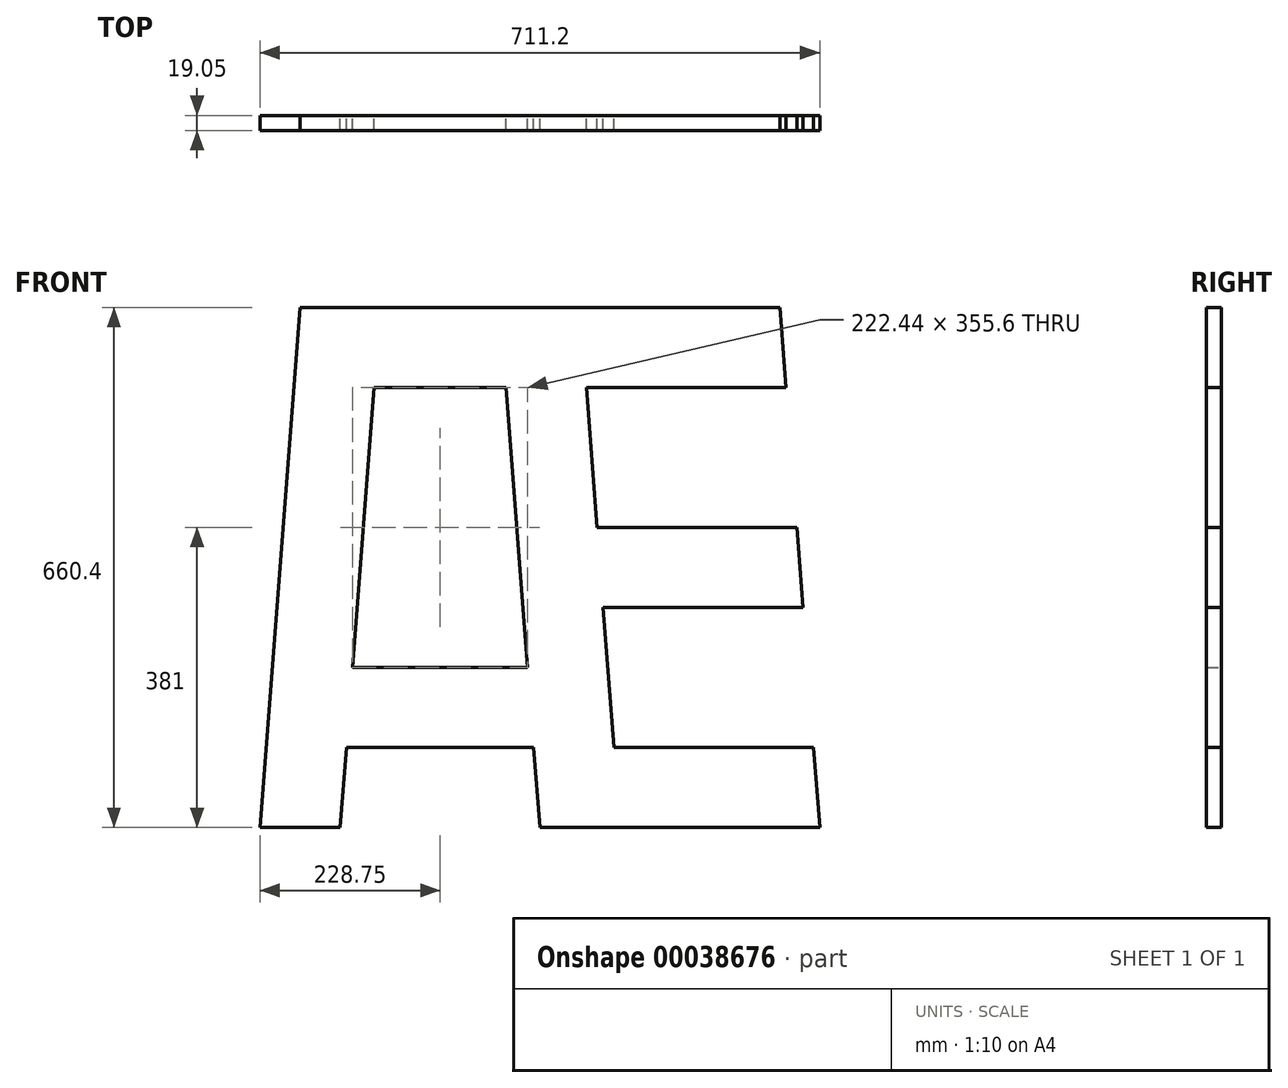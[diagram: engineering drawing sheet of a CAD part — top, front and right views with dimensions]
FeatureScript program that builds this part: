
annotation { "Feature Type Name" : "Feature", "Feature Type Description" : "" }
export const myFeature = defineFeature(function(context is Context, id is Id, definition is map)
    precondition{}
    {
        {
            var Q0;
            Q0=qCreatedBy(makeId("Front.planeOp"),FACE);
            var sketch = newSketch(context, id + "F0", { "sketchPlane" : qUnion([Q0])});
            skLineSegment(sketch, "E0", {"start": v(-304.8, 660.4) * mm, "end": v(-355.6, 0) * mm});
            skLineSegment(sketch, "E1", {"start": v(-355.6, 0) * mm, "end": v(355.6, 0) * mm});
            skLineSegment(sketch, "E2", {"start": v(355.6, 0) * mm, "end": v(304.8, 660.4) * mm});
            skLineSegment(sketch, "E3", {"start": v(304.8, 660.4) * mm, "end": v(-304.8, 660.4) * mm});
            skLineSegment(sketch, "E4", {"start": v(0, 660.4) * mm, "end": v(0, 0) * mm, "construction": true});
            skLineSegment(sketch, "E5", {"start": v(-253.7, 0) * mm, "end": v(-202.9, 660.4) * mm});
            skLineSegment(sketch, "E6", {"start": v(0, 0) * mm, "end": v(-50.8, 660.4) * mm});
            skLineSegment(sketch, "E7", {"start": v(51.1, 660.4) * mm, "end": v(101.9, 0) * mm});
            skLineSegment(sketch, "E8", {"start": v(58.92, 558.8) * mm, "end": v(312.62, 558.8) * mm});
            skLineSegment(sketch, "E9", {"start": v(76.5, 330.2) * mm, "end": v(330.2, 330.2) * mm, "construction": true});
            skLineSegment(sketch, "E10", {"start": v(72.6, 381) * mm, "end": v(326.3, 381) * mm});
            skLineSegment(sketch, "E11", {"start": v(80.4, 279.4) * mm, "end": v(334.1, 279.4) * mm});
            skLineSegment(sketch, "E12", {"start": v(94.08, 101.6) * mm, "end": v(347.78, 101.6) * mm});
            skLineSegment(sketch, "E13", {"start": v(-210.72, 558.8) * mm, "end": v(-42.98, 558.8) * mm});
            skLineSegment(sketch, "E14", {"start": v(-7.82, 101.6) * mm, "end": v(-245.88, 101.6) * mm});
            skLineSegment(sketch, "E15", {"start": v(-238.07, 203.2) * mm, "end": v(-15.63, 203.2) * mm});
            skSolve(sketch);
        }
        {
            var Q0;
            {var subQ0=sQuery(id+"F0.wireOp",EDGE,"E8");Q0=makeQuery(id+"F0.imprint","IMPRINT",FACE,{"disambiguationData":[TD([[makeQuery(id+"F0.imprint","IMPRINT",EDGE,{"derivedFrom":subQ0}),1.0]])]});}
            var Q1;
            {var subQ0=sQuery(id+"F0.wireOp",EDGE,"E12");Q1=makeQuery(id+"F0.imprint","IMPRINT",FACE,{"disambiguationData":[TD([[makeQuery(id+"F0.imprint","IMPRINT",EDGE,{"derivedFrom":subQ0}),-1.0]])]});}
            var Q2;
            {var subQ1=sQuery(id+"F0.wireOp",EDGE,"E14");Q2=makeQuery(id+"F0.imprint","IMPRINT",FACE,{"disambiguationData":[TD([[makeQuery(id+"F0.imprint","IMPRINT",EDGE,{"derivedFrom":subQ1}),-1.0]])]});}
            var Q3;
            {var subQ1=sQuery(id+"F0.wireOp",EDGE,"E10");Q3=makeQuery(id+"F0.imprint","IMPRINT",FACE,{"disambiguationData":[TD([[makeQuery(id+"F0.imprint","IMPRINT",EDGE,{"derivedFrom":subQ1}),-1.0]])]});}
            var Q4;
            {var subQ4=sQuery(id+"F0.wireOp",EDGE,"E0");Q4=makeQuery(id+"F0.imprint","IMPRINT",FACE,{"disambiguationData":[TD([[makeQuery(id+"F0.imprint","IMPRINT",EDGE,{"derivedFrom":subQ4}),1.0]])]});}
            var Q5;
            {var subQ2=sQuery(id+"F0.wireOp",EDGE,"E1");var subQ6=sQuery(id+"F0.wireOp",EDGE,"E6");var subQ9=makeQuery(id+"F0.imprint","INTERSECT",VERTEX,{"derivedFrom":[subQ2,subQ6]});Q5=makeQuery(id+"F0.imprint","IMPRINT",FACE,{"disambiguationData":[TD([[makeQuery(id+"F0.imprint","IMPRINT",EDGE,{"disambiguationData":[TD([[subQ9,-1.0]])],"derivedFrom":subQ2}),1.0]])]});}
            var Q6;
            {var subQ0=sQuery(id+"F0.wireOp",EDGE,"E13");Q6=makeQuery(id+"F0.imprint","IMPRINT",FACE,{"disambiguationData":[TD([[makeQuery(id+"F0.imprint","IMPRINT",EDGE,{"derivedFrom":subQ0}),1.0]])]});}
            extrude(context, id + "F1", {"entities" : qUnion([Q0, Q1, Q2, Q3, Q4, Q5, Q6]), "depth" : 19.05 * mm});
        }
    });
